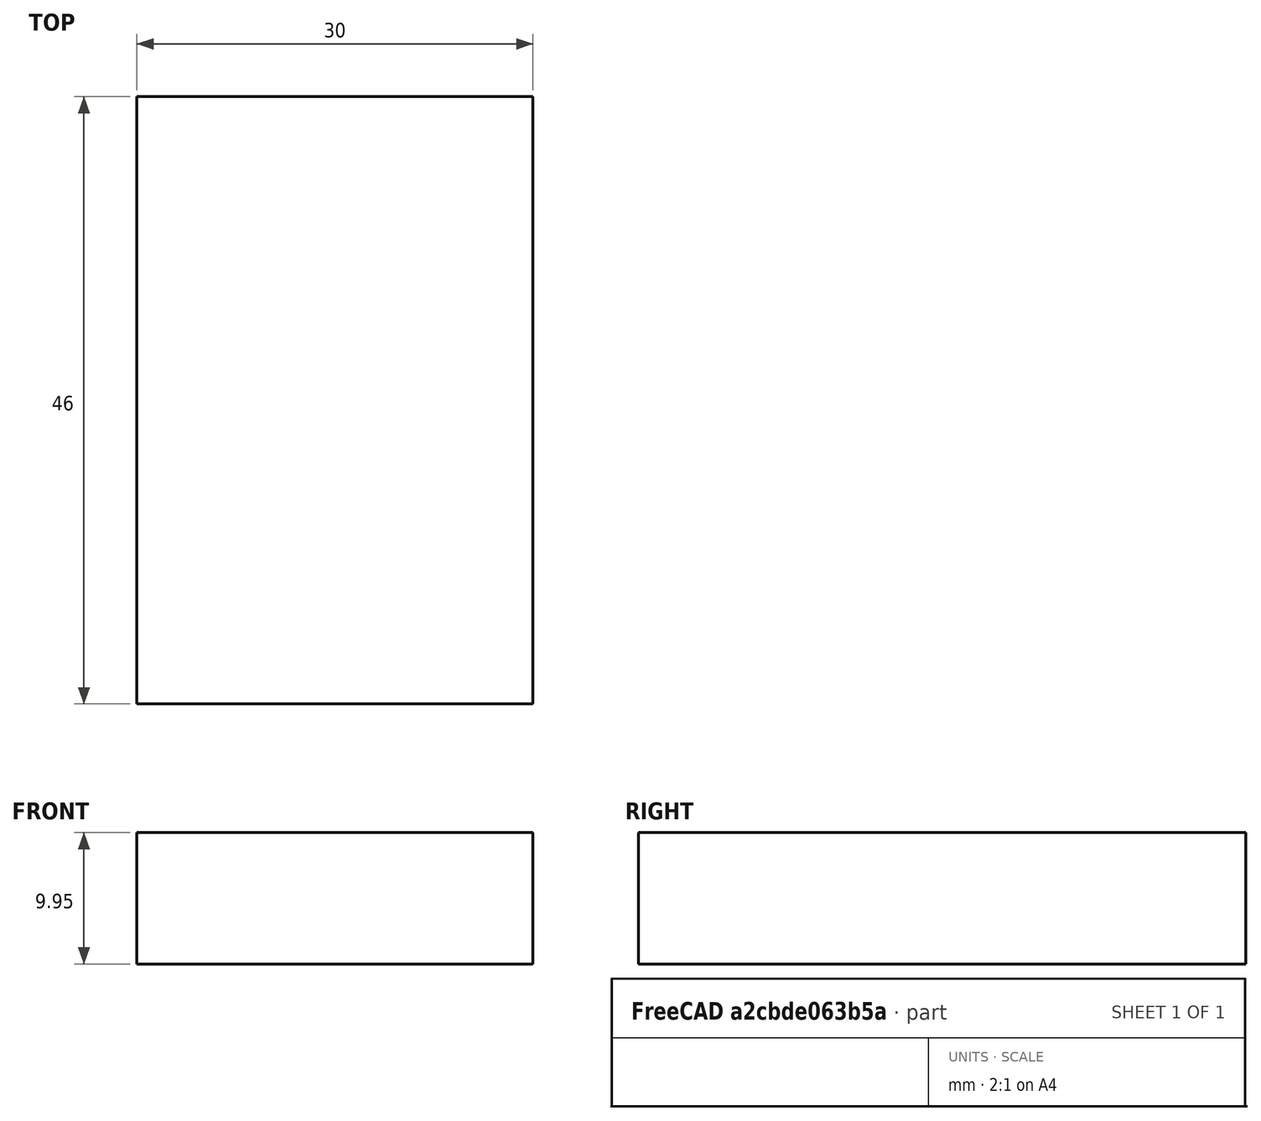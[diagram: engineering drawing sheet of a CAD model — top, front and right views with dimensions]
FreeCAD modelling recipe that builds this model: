
FCSTD DOCUMENT  (FreeCAD 1.0R39109 (Git))
Label: Rotor_Magnet
License: All rights reserved
LicenseURL: http://en.wikipedia.org/wiki/All_rights_reserved
objects: Part::Box×1, Spreadsheet::Sheet×1
note: 1 computed .brp shape members not serialized (recipe doc carries the construction recipe); baked Part::Feature solids carry a one-line shape summary decoded from their .brp
EXTERNAL_REF file=../../Master_of_Puppets.FCStd obj=Alternator
EXTERNAL_REF file=../../Master_of_Puppets.FCStd obj=Spreadsheet

FEATURE [Part::Box] Box  label="Rotor_Magnet"
  AttacherType = Attacher::AttachEngine3D
  Height = 9.95
  Length = 30
  Width = 46
  expr: Height = Spreadsheet.MagnetThickness
  expr: Length = Spreadsheet.MagnetWidth
  expr: Width = Spreadsheet.MagnetLength
FEATURE [Spreadsheet::Sheet] Spreadsheet
  cells = A1='Inputs; A2='MagnetLength; B2(MagnetLength)==Master_of_Puppets#Spreadsheet.MagnetLength; A3='MagnetWidth; B3(MagnetWidth)==Master_of_Puppets#Spreadsheet.MagnetWidth; A4='MagnetMaterial; B4(MagnetMaterial)==Master_of_Puppets#Alternator.MagnetMaterial; A5='ThicknessOffset; B5(ThicknessOffset)==MagnetMaterial == <<Ferrite C8>> ? 0 : 0.05; C5='Make magnet slightly thinner than resin cast to fix z-fighting rendering issue.; A6='MagnetThickness; B6(MagnetThickness)==Master_of_Puppets#Spreadsheet.MagnetThickness - ThicknessOffset
